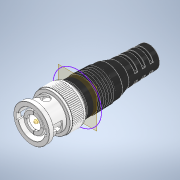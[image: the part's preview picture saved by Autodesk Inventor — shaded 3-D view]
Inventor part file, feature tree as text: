
AUTODESK INVENTOR PART (.ipt)
format: ipt  version: 2022 (Build 260153000, 153)  size: 1,217,536 bytes
history: native  units: in
note: dims shown in document units (in); Inventor stores cm internally (conversion verified against a paired STEP export)
features: other x4, extrude x2, sketch x2, plane x1, fillet x1
ambient origin geometry x8: Origin, YZ Plane, XZ Plane, XY Plane, X Axis, Y Axis, Z Axis, Center Point
bodies: Solid1 (feature_tree), Solid2 (feature_tree), Solid3 (feature_tree), Solid4 (feature_tree), Solid5 (feature_tree)
feature tree (10):
  plane  "Work Plane1"
  extrude  "Extrusion1"  Depth=1.3563in TaperAngle=0.0deg
  extrude  "Extrusion2"  [1 undecoded]
  sketch  "Sketch2"  dims[d0=-0.6693in d1=1.3563in d2=0.0in]
  sketch  "Sketch3"  dims[d3=1.3563in d4=0.0in]
  other  "Boss-Extrude2"
  other  "Boss-Extrude5"
  other  "Cut-Extrude2"
  fillet  "Fillet5"  [1 undecoded]
  other  "Boss-Extrude7"
note: 2 required parameter values undecoded (feature->parameter linkage not recoverable at this tier; creation-order binding heuristic only, values carry confidence <= 0.55)
